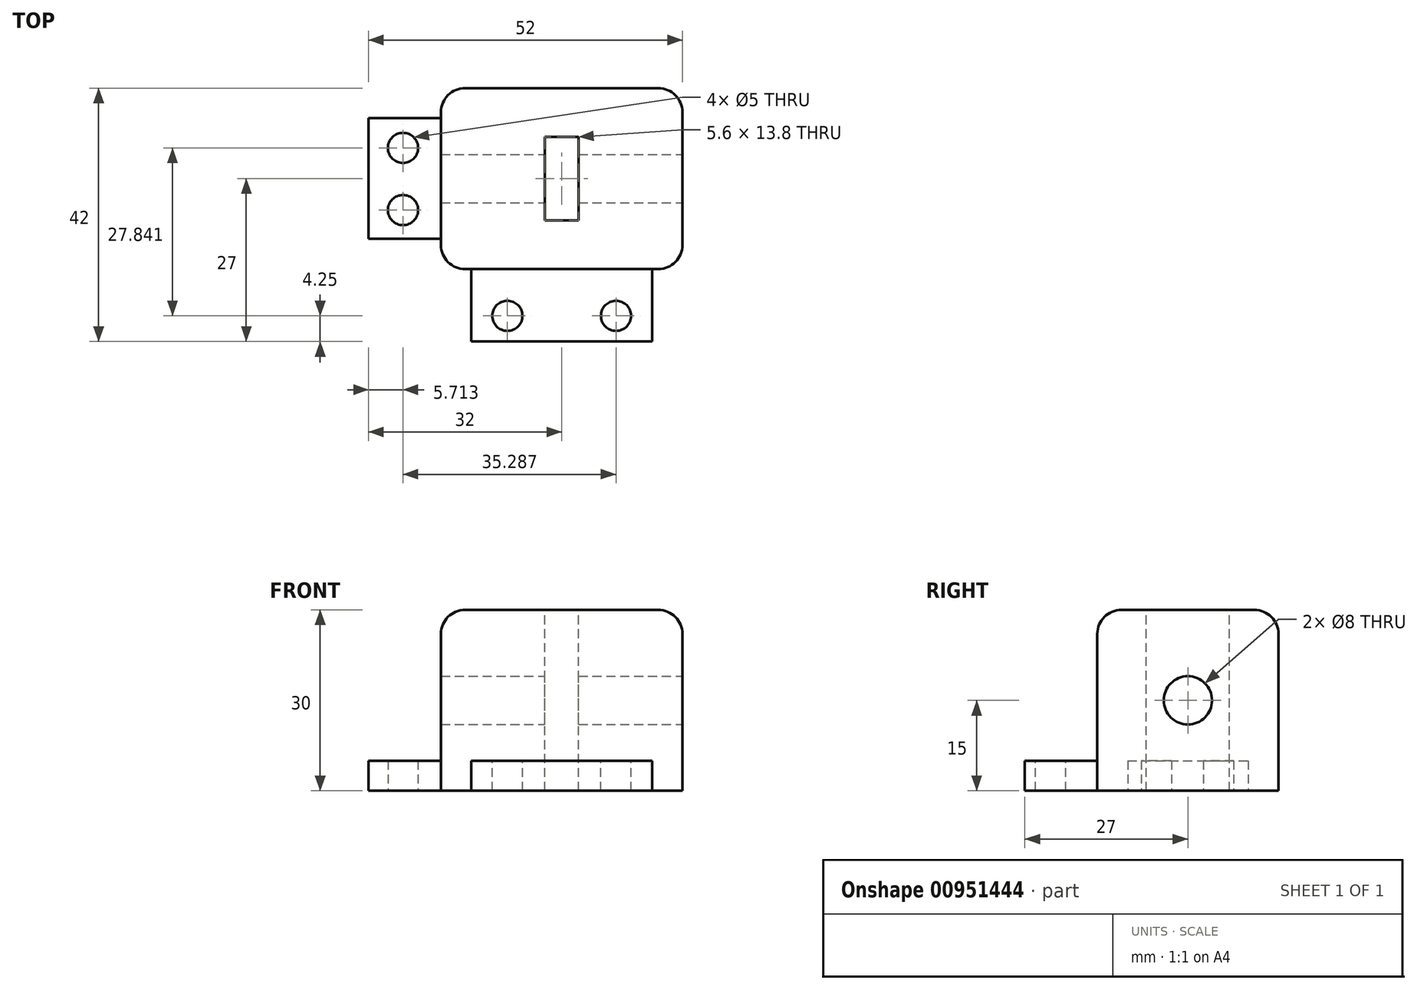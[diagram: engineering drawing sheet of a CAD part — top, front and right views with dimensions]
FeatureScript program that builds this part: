
annotation { "Feature Type Name" : "Feature", "Feature Type Description" : "" }
export const myFeature = defineFeature(function(context is Context, id is Id, definition is map)
    precondition{}
    {
        {
            var Q0;
            Q0=qCreatedBy(makeId("Top.planeOp"),FACE);
            var sketch = newSketch(context, id + "F0", { "sketchPlane" : qUnion([Q0])});
            skLineSegment(sketch, "E0.bottom", {"start": v(20, -15) * mm, "end": v(-20, -15) * mm});
            skLineSegment(sketch, "E0.top", {"start": v(20, 15) * mm, "end": v(-20, 15) * mm});
            skLineSegment(sketch, "E0.left", {"start": v(20, -15) * mm, "end": v(20, 15) * mm});
            skLineSegment(sketch, "E0.right", {"start": v(-20, -15) * mm, "end": v(-20, 15) * mm});
            skPoint(sketch, "E0.middle", {"position": v(0, 0) * mm});
            skLineSegment(sketch, "E1", {"start": v(-15, -15) * mm, "end": v(-15, -27) * mm});
            skLineSegment(sketch, "E2", {"start": v(-15, -27) * mm, "end": v(15, -27) * mm});
            skLineSegment(sketch, "E3", {"start": v(15, -27) * mm, "end": v(15, -15) * mm});
            skLineSegment(sketch, "E4.bottom", {"start": v(-20, -9.98) * mm, "end": v(-32, -9.98) * mm});
            skLineSegment(sketch, "E4.top", {"start": v(-20, 10.02) * mm, "end": v(-32, 10.02) * mm});
            skLineSegment(sketch, "E4.left", {"start": v(-20, -9.98) * mm, "end": v(-20, 10.02) * mm});
            skLineSegment(sketch, "E4.right", {"start": v(-32, -9.98) * mm, "end": v(-32, 10.02) * mm});
            skCircle(sketch, "E5", {"center": v(-26.29, -5.22) * mm, "radius": 2.5 * mm});
            skCircle(sketch, "E6", {"center": v(-26.29, 5.1) * mm, "radius": 2.5 * mm});
            skSolve(sketch);
        }
        {
            var Q0;
            {var subQ0=sQuery(id+"F0.wireOp",EDGE,"E0.top");Q0=makeQuery(id+"F0.imprint","IMPRINT",FACE,{"disambiguationData":[TD([[makeQuery(id+"F0.imprint","IMPRINT",EDGE,{"derivedFrom":subQ0}),1.0]])]});}
            extrude(context, id + "F1", {"entities" : qUnion([Q0]), "depth" : 30 * mm, "offsetDistance" : 25 * mm});
        }
        {
            var Q0;
            {var subQ2=sQuery(id+"F0.wireOp",EDGE,"E1");Q0=makeQuery(id+"F0.imprint","IMPRINT",FACE,{"disambiguationData":[TD([[makeQuery(id+"F0.imprint","IMPRINT",EDGE,{"derivedFrom":subQ2}),1.0]])]});}
            var Q1;
            {var subQ0=sQuery(id+"F0.wireOp",EDGE,"1XpmxUhX-fvAz-m8h3-Jup1-kxhkT4kGMUfl");Q1=makeQuery(id+"F0.imprint","IMPRINT",FACE,{"disambiguationData":[TD([[makeQuery(id+"F0.imprint","IMPRINT",EDGE,{"derivedFrom":subQ0}),-1.0]])]});}
            extrude(context, id + "F2", {"entities" : qUnion([Q0, Q1]), "operationType" : NewBodyOperationType.ADD, "depth" : 5 * mm, "offsetDistance" : 25 * mm});
        }
        {
            var Q0;
            Q0=makeQuery(id+"F1.opExtrude","SWEPT_FACE",FACE,{"disambiguationData":[OSD([sQuery(id+"F0.wireOp",EDGE,"E0.left")])]});
            var sketch = newSketch(context, id + "F3", { "sketchPlane" : qUnion([Q0])});
            skCircle(sketch, "E7", {"center": v(0, 15) * mm, "radius": 4 * mm});
            skPoint(sketch, "E7.centerSnap0", {"position": v(-15, 15) * mm});
            skPoint(sketch, "E7.centerSnap1", {"position": v(0, 0) * mm});
            skSolve(sketch);
        }
        {
            var Q0;
            Q0=makeQuery(id+"F3.imprint","IMPRINT",FACE,{"disambiguationData":[TD([[makeQuery(id+"F3.imprint","IMPRINT",EDGE,{"derivedFrom":sQuery(id+"F3.wireOp",EDGE,"E7")}),1.0]])]});
            extrude(context, id + "F4", {"entities" : qUnion([Q0]), "operationType" : NewBodyOperationType.REMOVE, "endBound" : BoundingType.THROUGH_ALL, "oppositeDirection" : true, "depth" : 25 * mm, "offsetDistance" : 25 * mm});
        }
        {
            var Q0;
            Q0=makeQuery(id+"F2.opExtrude","CAP_FACE",FACE,{"disambiguationData":[OSD([sQuery(id+"F0.wireOp",EDGE,"E0.bottom"),sQuery(id+"F0.wireOp",EDGE,"E1"),sQuery(id+"F0.wireOp",EDGE,"E2"),sQuery(id+"F0.wireOp",EDGE,"E3")])],"isStart":false});
            var sketch = newSketch(context, id + "F5", { "sketchPlane" : qUnion([Q0])});
            skCircle(sketch, "E8", {"center": v(9, -22.75) * mm, "radius": 2.5 * mm});
            skCircle(sketch, "E9", {"center": v(-9, -22.75) * mm, "radius": 2.5 * mm});
            skSolve(sketch);
        }
        {
            var Q0;
            Q0=makeQuery(id+"F5.imprint","IMPRINT",FACE,{"disambiguationData":[TD([[makeQuery(id+"F5.imprint","IMPRINT",EDGE,{"derivedFrom":sQuery(id+"F5.wireOp",EDGE,"E8")}),1.0]])]});
            var Q1;
            Q1=makeQuery(id+"F5.imprint","IMPRINT",FACE,{"disambiguationData":[TD([[makeQuery(id+"F5.imprint","IMPRINT",EDGE,{"derivedFrom":sQuery(id+"F5.wireOp",EDGE,"E9")}),1.0]])]});
            extrude(context, id + "F6", {"entities" : qUnion([Q0, Q1]), "operationType" : NewBodyOperationType.REMOVE, "endBound" : BoundingType.THROUGH_ALL, "oppositeDirection" : true, "depth" : 25 * mm, "offsetDistance" : 25 * mm});
        }
        {
            var Q0;
            Q0=makeQuery(id+"F1.opExtrude","CAP_FACE",FACE,{"disambiguationData":[OSD([sQuery(id+"F0.wireOp",EDGE,"E0.bottom"),sQuery(id+"F0.wireOp",EDGE,"E0.top"),sQuery(id+"F0.wireOp",EDGE,"E0.left"),sQuery(id+"F0.wireOp",EDGE,"E0.right")])],"isStart":false});
            var sketch = newSketch(context, id + "F7", { "sketchPlane" : qUnion([Q0])});
            skLineSegment(sketch, "E10.bottom", {"start": v(-2.8, -6.9) * mm, "end": v(2.8, -6.9) * mm});
            skLineSegment(sketch, "E10.top", {"start": v(-2.8, 6.9) * mm, "end": v(2.8, 6.9) * mm});
            skLineSegment(sketch, "E10.left", {"start": v(-2.8, -6.9) * mm, "end": v(-2.8, 6.9) * mm});
            skLineSegment(sketch, "E10.right", {"start": v(2.8, -6.9) * mm, "end": v(2.8, 6.9) * mm});
            skPoint(sketch, "E10.middle", {"position": v(0, 0) * mm});
            skSolve(sketch);
        }
        {
            var Q0;
            Q0=makeQuery(id+"F7.imprint","IMPRINT",FACE,{"disambiguationData":[TD([[makeQuery(id+"F7.imprint","IMPRINT",EDGE,{"derivedFrom":sQuery(id+"F7.wireOp",EDGE,"E10.bottom")}),1.0]])]});
            extrude(context, id + "F8", {"entities" : qUnion([Q0]), "operationType" : NewBodyOperationType.REMOVE, "endBound" : BoundingType.THROUGH_ALL, "oppositeDirection" : true, "depth" : 25 * mm, "offsetDistance" : 25 * mm});
        }
        {
            var Q0;
            {var subQ1=sQuery(id+"F0.wireOp",EDGE,"E4.bottom");Q0=makeQuery(id+"F0.imprint","IMPRINT",FACE,{"disambiguationData":[TD([[makeQuery(id+"F0.imprint","IMPRINT",EDGE,{"derivedFrom":subQ1}),-1.0]])]});}
            extrude(context, id + "F9", {"entities" : qUnion([Q0]), "operationType" : NewBodyOperationType.ADD, "depth" : 5 * mm, "offsetDistance" : 25 * mm});
        }
        {
            var Q0;
            Q0=makeQuery(id+"F9.opExtrude","CAP_EDGE",EDGE,{"disambiguationData":[OSD([sQuery(id+"F0.wireOp",EDGE,"E0.right")])],"isStart":false});
            var Q1;
            Q1=makeQuery(id+"F1.opExtrude","SWEPT_EDGE",EDGE,{"disambiguationData":[OSD([sQuery(id+"F0.wireOp",EDGE,"E0.top"),sQuery(id+"F0.wireOp",EDGE,"E0.right")])]});
            var Q2;
            Q2=makeQuery(id+"F1.opExtrude","CAP_EDGE",EDGE,{"disambiguationData":[OSD([sQuery(id+"F0.wireOp",EDGE,"E0.right")])],"isStart":false});
            var Q3;
            Q3=makeQuery(id+"F1.opExtrude","SWEPT_EDGE",EDGE,{"disambiguationData":[OSD([sQuery(id+"F0.wireOp",EDGE,"E0.bottom"),sQuery(id+"F0.wireOp",EDGE,"E0.right")])]});
            var Q4;
            Q4=makeQuery(id+"F2.opExtrude","CAP_EDGE",EDGE,{"disambiguationData":[OSD([sQuery(id+"F0.wireOp",EDGE,"E0.bottom")])],"isStart":false});
            var Q5;
            Q5=makeQuery(id+"F1.opExtrude","CAP_EDGE",EDGE,{"disambiguationData":[OSD([sQuery(id+"F0.wireOp",EDGE,"E0.bottom")])],"isStart":false});
            var Q6;
            Q6=makeQuery(id+"F1.opExtrude","SWEPT_EDGE",EDGE,{"disambiguationData":[OSD([sQuery(id+"F0.wireOp",EDGE,"E0.bottom"),sQuery(id+"F0.wireOp",EDGE,"E0.left")])]});
            var Q7;
            Q7=makeQuery(id+"F1.opExtrude","CAP_EDGE",EDGE,{"disambiguationData":[OSD([sQuery(id+"F0.wireOp",EDGE,"E0.left")])],"isStart":false});
            var Q8;
            Q8=makeQuery(id+"F1.opExtrude","CAP_EDGE",EDGE,{"disambiguationData":[OSD([sQuery(id+"F0.wireOp",EDGE,"E0.top")])],"isStart":false});
            var Q9;
            Q9=makeQuery(id+"F1.opExtrude","SWEPT_EDGE",EDGE,{"disambiguationData":[OSD([sQuery(id+"F0.wireOp",EDGE,"E0.top"),sQuery(id+"F0.wireOp",EDGE,"E0.left")])]});
            fillet(context, id + "F10", {"entities" : qUnion([Q0, Q1, Q2, Q3, Q4, Q5, Q6, Q7, Q8, Q9]), "radius" : 4 * mm, "tangentPropagation" : true, "allowEdgeOverflow" : false});
        }
    });
